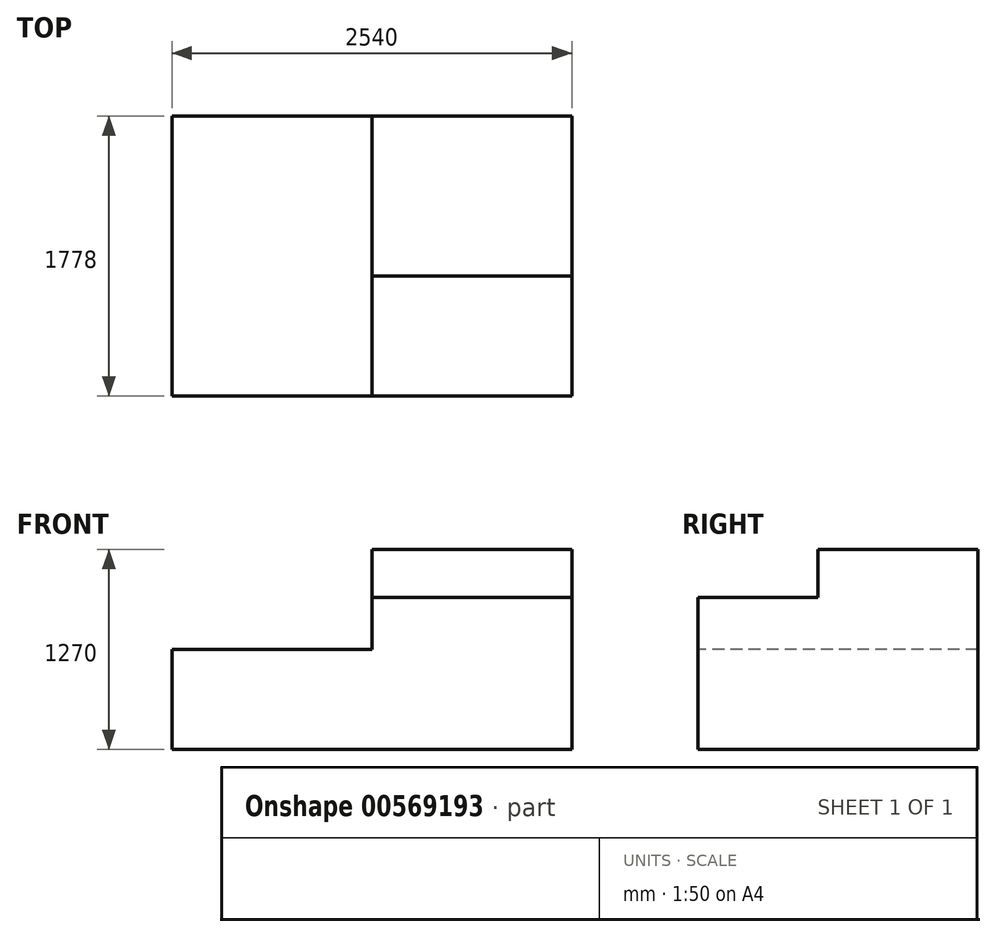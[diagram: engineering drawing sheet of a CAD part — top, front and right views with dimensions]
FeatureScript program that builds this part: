
annotation { "Feature Type Name" : "Feature", "Feature Type Description" : "" }
export const myFeature = defineFeature(function(context is Context, id is Id, definition is map)
    precondition{}
    {
        {
            var Q0;
            Q0=qCreatedBy(makeId("Front.planeOp"),FACE);
            var sketch = newSketch(context, id + "F0", { "sketchPlane" : qUnion([Q0])});
            skLineSegment(sketch, "E0", {"start": v(0, 0) * mm, "end": v(2540, 0) * mm});
            skLineSegment(sketch, "E1", {"start": v(2540, 0) * mm, "end": v(2540, 965.2) * mm});
            skLineSegment(sketch, "E2", {"start": v(2540, 965.2) * mm, "end": v(1270, 965.2) * mm});
            skLineSegment(sketch, "E3", {"start": v(1270, 965.2) * mm, "end": v(1270, 635) * mm});
            skLineSegment(sketch, "E4", {"start": v(1270, 635) * mm, "end": v(0, 635) * mm});
            skLineSegment(sketch, "E5", {"start": v(0, 635) * mm, "end": v(0, 0) * mm});
            skSolve(sketch);
        }
        {
            var Q0;
            Q0=makeQuery(id+"F0.imprint","IMPRINT",FACE,{"disambiguationData":[TD([[makeQuery(id+"F0.imprint","IMPRINT",EDGE,{"derivedFrom":sQuery(id+"F0.wireOp",EDGE,"E0")}),1.0]])]});
            extrude(context, id + "F1", {"entities" : qUnion([Q0]), "oppositeDirection" : true, "depth" : 1778 * mm, "offsetDistance" : 25.4 * mm});
        }
        {
            var Q0;
            Q0=makeQuery(id+"F1.opExtrude","SWEPT_FACE",FACE,{"disambiguationData":[OSD([sQuery(id+"F0.wireOp",EDGE,"E2")])]});
            var sketch = newSketch(context, id + "F2", { "sketchPlane" : qUnion([Q0])});
            skLineSegment(sketch, "E6", {"start": v(2540, 1778) * mm, "end": v(2540, 762) * mm});
            skLineSegment(sketch, "E7", {"start": v(2540, 762) * mm, "end": v(1270, 762) * mm});
            skLineSegment(sketch, "E8", {"start": v(1270, 762) * mm, "end": v(1270, 1778) * mm});
            skLineSegment(sketch, "E9", {"start": v(1270, 1778) * mm, "end": v(2540, 1778) * mm});
            skSolve(sketch);
        }
        {
            var Q0;
            Q0=makeQuery(id+"F2.imprint","IMPRINT",FACE,{"disambiguationData":[TD([[makeQuery(id+"F2.imprint","IMPRINT",EDGE,{"derivedFrom":sQuery(id+"F2.wireOp",EDGE,"E6")}),-1.0]])]});
            extrude(context, id + "F3", {"entities" : qUnion([Q0]), "operationType" : NewBodyOperationType.ADD, "depth" : 304.8 * mm, "offsetDistance" : 25.4 * mm});
        }
    });
